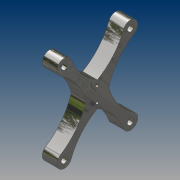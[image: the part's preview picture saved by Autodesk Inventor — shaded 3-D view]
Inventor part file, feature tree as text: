
AUTODESK INVENTOR PART (.ipt)
format: ipt  version: 2021 (Build 250183000, 183)  size: 152,576 bytes
history: native  units: mm
features: sketch x3, hole x2, extrude x1, projected_geometry x1
ambient origin geometry x8: Origin, YZ Plane, XZ Plane, XY Plane, X Axis, Y Axis, Z Axis, Center Point
bodies: Solid1 (feature_tree)
feature tree (7):
  extrude  "Extrusion1"  Depth=45.0mm
  hole  "Hole1"  [1 undecoded]
  hole  "Hole2"  [1 undecoded]
  sketch  "Sketch1"  dims[d0=55.0mm d1=45.0mm]
  sketch  "Sketch2"  dims[d2=10.0mm d3=15.0mm]
  projected_geometry  "Projected Loop1"
  sketch  "Sketch3"  dims[d4=41.0mm d5=10.0mm d6=0.0mm d7=4.2mm d8=6.0mm d9=4.0mm d10=2.0mm d11=90.0deg d12=8.0mm d13=20.594885mm d14=10.0mm d15=1.8mm d16=6.0mm d17=4.0mm d18=2.0mm d19=90.0deg d20=8.0mm d21=20.594885mm]
note: 2 required parameter values undecoded (feature->parameter linkage not recoverable at this tier; creation-order binding heuristic only, values carry confidence <= 0.55)
